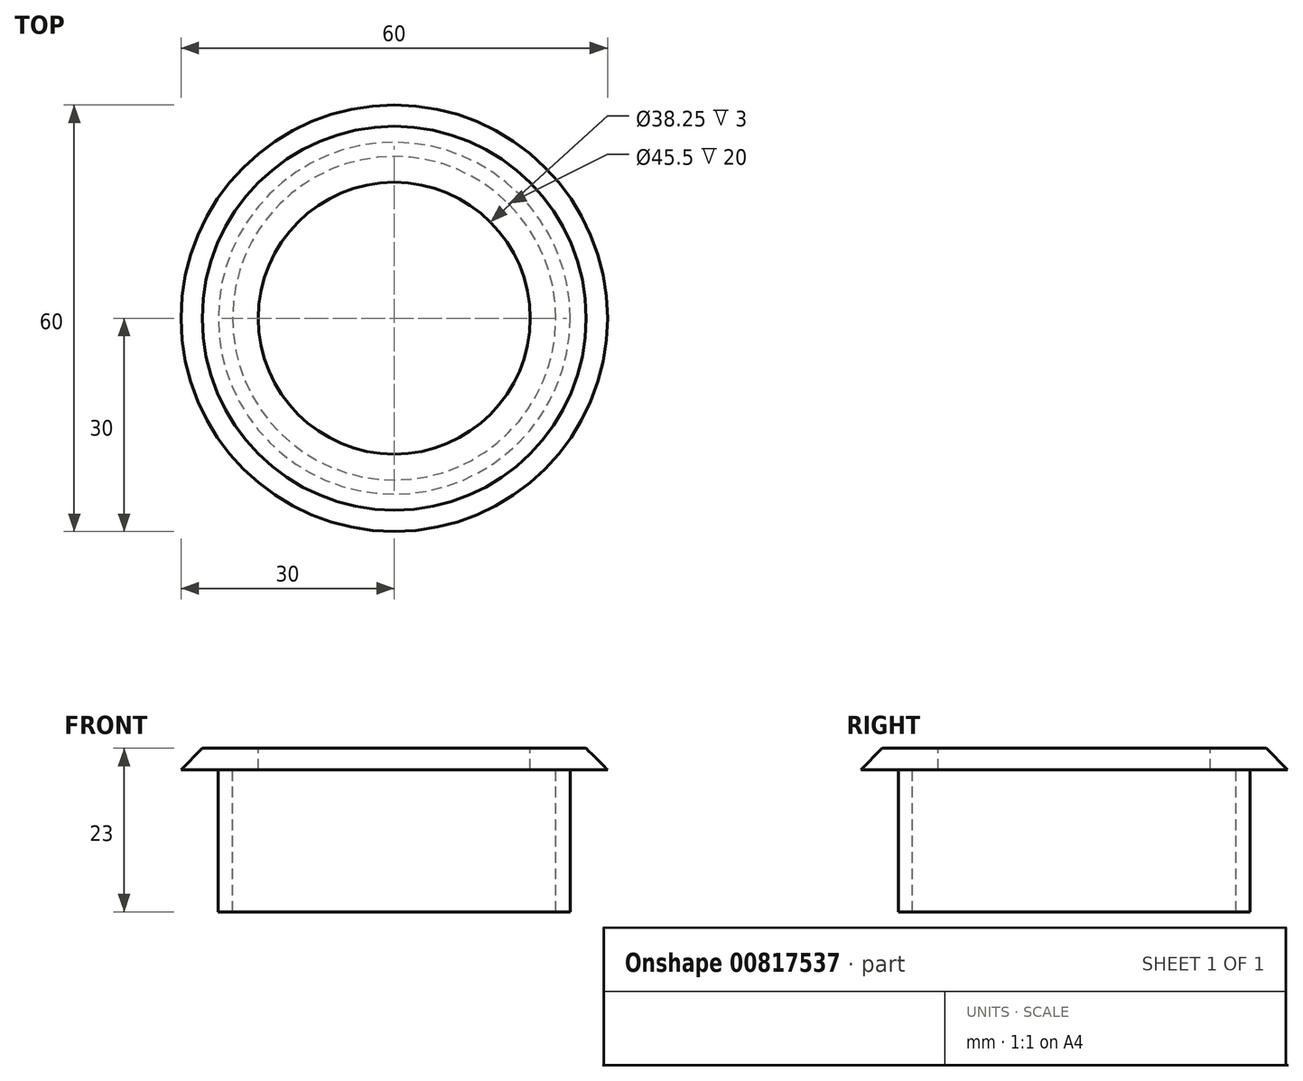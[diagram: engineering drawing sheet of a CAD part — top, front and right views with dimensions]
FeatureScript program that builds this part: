
annotation { "Feature Type Name" : "Feature", "Feature Type Description" : "" }
export const myFeature = defineFeature(function(context is Context, id is Id, definition is map)
    precondition{}
    {
        {
            var Q0;
            Q0=qCreatedBy(makeId("Top.planeOp"),FACE);
            var sketch = newSketch(context, id + "F0", { "sketchPlane" : qUnion([Q0])});
            skCircle(sketch, "E0", {"center": v(0, 0) * mm, "radius": 30 * mm});
            skSolve(sketch);
        }
        {
            var Q0;
            Q0 = qSketchRegion(id + "F0", true);
            extrude(context, id + "F1", {"entities" : qUnion([Q0]), "depth" : 3 * mm, "offsetDistance" : 25 * mm});
        }
        {
            var Q0;
            Q0=makeQuery(id+"F1.opExtrude","CAP_EDGE",EDGE,{"disambiguationData":[OSD([sQuery(id+"F0.wireOp",EDGE,"E0")])],"isStart":false});
            chamfer(context, id + "F2", {"entities" : qUnion([Q0]), "width" : 3 * mm, "tangentPropagation" : true});
        }
        {
            var Q0;
            Q0=makeQuery(id+"F1.opExtrude","CAP_FACE",FACE,{"disambiguationData":[OSD([sQuery(id+"F0.wireOp",EDGE,"E0")])],"isStart":false});
            var sketch = newSketch(context, id + "F3", { "sketchPlane" : qUnion([Q0])});
            skCircle(sketch, "E1", {"center": v(0, 0) * mm, "radius": 19.12 * mm});
            skSolve(sketch);
        }
        {
            var Q0;
            Q0 = qSketchRegion(id + "F3", true);
            extrude(context, id + "F4", {"entities" : qUnion([Q0]), "operationType" : NewBodyOperationType.REMOVE, "endBound" : BoundingType.THROUGH_ALL, "oppositeDirection" : true, "depth" : 25 * mm, "offsetDistance" : 25 * mm});
        }
        {
            var Q0;
            Q0=makeQuery(id+"F1.opExtrude","CAP_FACE",FACE,{"disambiguationData":[OSD([sQuery(id+"F0.wireOp",EDGE,"E0")])],"isStart":true});
            var sketch = newSketch(context, id + "F5", { "sketchPlane" : qUnion([Q0])});
            skCircle(sketch, "E2", {"center": v(0, 0) * mm, "radius": 24.75 * mm});
            skCircle(sketch, "E3", {"center": v(0, 0) * mm, "radius": 22.75 * mm});
            skSolve(sketch);
        }
        {
            var Q0;
            Q0 = qSketchRegion(id + "F5", true);
            extrude(context, id + "F6", {"entities" : qUnion([Q0]), "operationType" : NewBodyOperationType.ADD, "depth" : 20 * mm, "offsetDistance" : 25 * mm});
        }
    });
